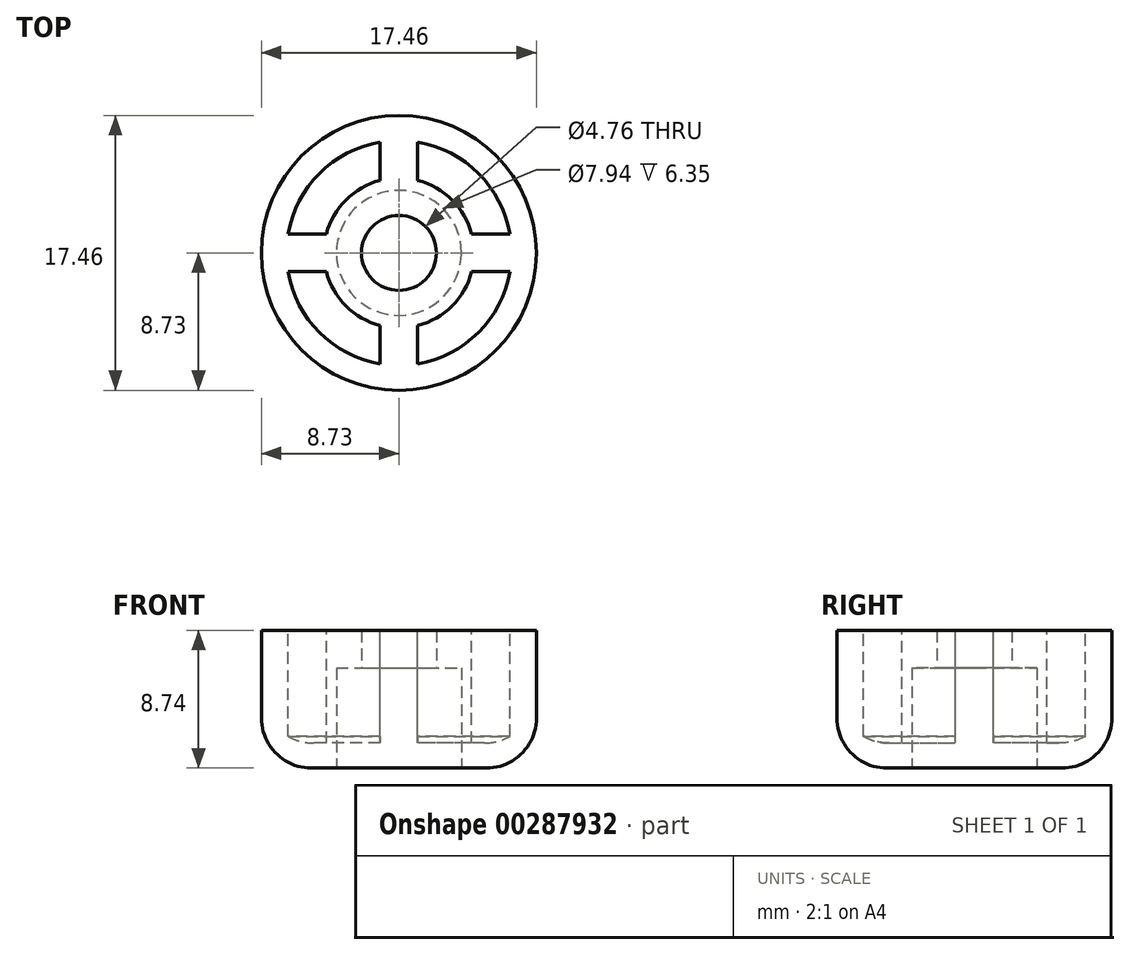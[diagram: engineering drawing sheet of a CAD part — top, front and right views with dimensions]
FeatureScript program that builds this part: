
annotation { "Feature Type Name" : "Feature", "Feature Type Description" : "" }
export const myFeature = defineFeature(function(context is Context, id is Id, definition is map)
    precondition{}
    {
        {
            var Q0;
            Q0=qCreatedBy(makeId("Top.planeOp"),FACE);
            var sketch = newSketch(context, id + "F0", { "sketchPlane" : qUnion([Q0])});
            skCircle(sketch, "E0", {"center": v(0, 0) * mm, "radius": 8.73 * mm});
            skSolve(sketch);
        }
        {
            var Q0;
            Q0=makeQuery(id+"F0.imprint","IMPRINT",FACE,{"disambiguationData":[TD([[makeQuery(id+"F0.imprint","IMPRINT",EDGE,{"derivedFrom":sQuery(id+"F0.wireOp",EDGE,"E0")}),1.0]])]});
            extrude(context, id + "F1", {"entities" : qUnion([Q0]), "depth" : 8.74 * mm, "offsetDistance" : 25.4 * mm});
        }
        {
            var Q0;
            Q0=makeQuery(id+"F1.opExtrude","CAP_EDGE",EDGE,{"disambiguationData":[OSD([sQuery(id+"F0.wireOp",EDGE,"E0")])],"isStart":true});
            fillet(context, id + "F2", {"entities" : qUnion([Q0]), "radius" : 3.17 * mm, "tangentPropagation" : true, "allowEdgeOverflow" : false});
        }
        {
            var Q0;
            Q0=makeQuery(id+"F1.opExtrude","CAP_FACE",FACE,{"disambiguationData":[OSD([sQuery(id+"F0.wireOp",EDGE,"E0")])],"isStart":true});
            var sketch = newSketch(context, id + "F3", { "sketchPlane" : qUnion([Q0])});
            skPoint(sketch, "E1", {"position": v(0, 0) * mm});
            skSolve(sketch);
        }
        {
            var Q0;
            Q0=sQuery(id+"F3.wireOp",VERTEX,"E1");
            var Q1;
            Q1=makeQuery(id+"F1.opExtrude","SWEPT_BODY",BODY,{"disambiguationData":[OSD([sQuery(id+"F0.wireOp",EDGE,"E0")])]});
            hole(context, id + "F4", {"style" : HoleStyle.C_BORE, "endStyle" : HoleEndStyle.BLIND, "holeDiameter" : 4.76 * mm, "cBoreDiameter" : 7.94 * mm, "cBoreDepth" : 6.35 * mm, "majorDiameter" : 4.17 * mm, "holeDepth" : 12.7 * mm, "isTappedThrough" : true, "tappedDepth" : 10.32 * mm, "tapClearance" : 3, "locations" : qUnion([Q0]), "scope" : qUnion([Q1])});
        }
        {
            var Q0;
            Q0=makeQuery(id+"F1.opExtrude","CAP_FACE",FACE,{"disambiguationData":[OSD([sQuery(id+"F0.wireOp",EDGE,"E0")])],"isStart":false});
            var sketch = newSketch(context, id + "F5", { "sketchPlane" : qUnion([Q0])});
            skCircle(sketch, "E2", {"center": v(0, 0) * mm, "radius": 4.76 * mm});
            skCircle(sketch, "E3", {"center": v(0, 0) * mm, "radius": 7.14 * mm});
            skLineSegment(sketch, "E4", {"start": v(-1.2, 7.04) * mm, "end": v(-1.2, 4.61) * mm});
            skLineSegment(sketch, "E5", {"start": v(1.2, 7.04) * mm, "end": v(1.2, 4.61) * mm});
            skLineSegment(sketch, "E6", {"start": v(4.61, 1.2) * mm, "end": v(7.04, 1.2) * mm});
            skLineSegment(sketch, "E7", {"start": v(4.61, -1.2) * mm, "end": v(7.04, -1.2) * mm});
            skLineSegment(sketch, "E8", {"start": v(-7.04, 1.2) * mm, "end": v(-4.61, 1.2) * mm});
            skLineSegment(sketch, "E9", {"start": v(-7.04, -1.2) * mm, "end": v(-4.61, -1.2) * mm});
            skLineSegment(sketch, "E10", {"start": v(-1.2, -7.04) * mm, "end": v(-1.2, -4.61) * mm});
            skLineSegment(sketch, "E11", {"start": v(1.2, -4.61) * mm, "end": v(1.2, -7.04) * mm});
            skLineSegment(sketch, "E12", {"start": v(0, 13.5) * mm, "end": v(0, -11.94) * mm, "construction": true});
            skLineSegment(sketch, "E13", {"start": v(-13.8, 0) * mm, "end": v(12.64, 0) * mm, "construction": true});
            skSolve(sketch);
        }
        {
            var Q0;
            {var subQ0=sQuery(id+"F5.wireOp",EDGE,"E4");Q0=makeQuery(id+"F5.imprint","IMPRINT",FACE,{"disambiguationData":[TD([[makeQuery(id+"F5.imprint","IMPRINT",EDGE,{"derivedFrom":subQ0}),-1.0]])]});}
            var Q1;
            {var subQ0=sQuery(id+"F5.wireOp",EDGE,"E5");Q1=makeQuery(id+"F5.imprint","IMPRINT",FACE,{"disambiguationData":[TD([[makeQuery(id+"F5.imprint","IMPRINT",EDGE,{"derivedFrom":subQ0}),1.0]])]});}
            var Q2;
            {var subQ0=sQuery(id+"F5.wireOp",EDGE,"E7");Q2=makeQuery(id+"F5.imprint","IMPRINT",FACE,{"disambiguationData":[TD([[makeQuery(id+"F5.imprint","IMPRINT",EDGE,{"derivedFrom":subQ0}),-1.0]])]});}
            var Q3;
            {var subQ0=sQuery(id+"F5.wireOp",EDGE,"E9");Q3=makeQuery(id+"F5.imprint","IMPRINT",FACE,{"disambiguationData":[TD([[makeQuery(id+"F5.imprint","IMPRINT",EDGE,{"derivedFrom":subQ0}),-1.0]])]});}
            var Q4;
            Q4=makeQuery(id+"F1.opExtrude","CAP_FACE",FACE,{"disambiguationData":[OSD([sQuery(id+"F0.wireOp",EDGE,"E0")])],"isStart":true});
            var Q5;
            Q5=makeQuery(id+"F1.opExtrude","SWEPT_BODY",BODY,{"disambiguationData":[OSD([sQuery(id+"F0.wireOp",EDGE,"E0")])]});
            extrude(context, id + "F6", {"entities" : qUnion([Q0, Q1, Q2, Q3]), "operationType" : NewBodyOperationType.REMOVE, "endBound" : BoundingType.UP_TO_BODY, "oppositeDirection" : true, "depth" : 25.4 * mm, "endBoundEntityFace" : qUnion([Q4]), "endBoundEntityBody" : qUnion([Q5]), "hasOffset" : true, "offsetDistance" : 1.59 * mm});
        }
    });
